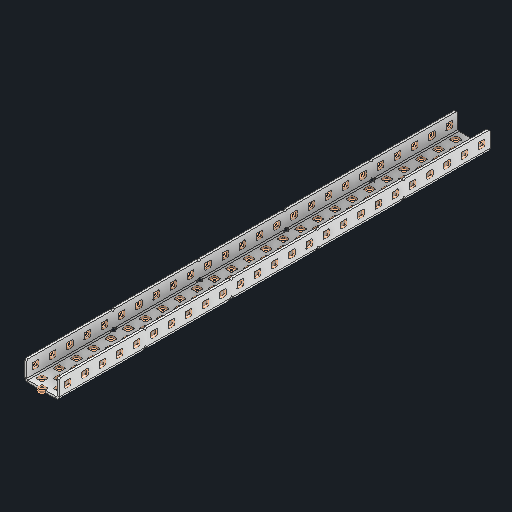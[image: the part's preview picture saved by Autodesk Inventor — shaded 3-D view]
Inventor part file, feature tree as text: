
AUTODESK INVENTOR PART (.ipt)
format: ipt  version: 2024 (Build 280153000, 153)  size: 2,036,224 bytes
history: native  units: in
note: dims shown in document units (in); Inventor stores cm internally (conversion verified against a paired STEP export)
features: other x256, sketch x5, sheet_metal_op x1
ambient origin geometry x8: Origin, YZ Plane, XZ Plane, XY Plane, X Axis, Y Axis, Z Axis, Center Point
bodies: Solid1 (feature_tree)
feature tree (262):
  other  "Alu C 1x2x1x25.ipt"
  other  "Solid1::Alu C 1x2x1x25.ipt"
  other  "TaggingFeature1"
  sketch  "Sketch1"  dims[d0=0.3937in]
  sketch  "Sketch2"  dims[d1=0.0625in]
  sketch  "Sketch3"
  other  "Flange Pattern Sketch"
  sketch  "Sketch9"
  sheet_metal_op  "Body Pattern Sketch"
  other  "Arc Length"
  sketch  "Sketch14"
  other  "Flange Pattern Plane"
  other  "Srf1"
  other  "Srf2"
  other  "Srf3"
  other  "Srf4"
  other  "Srf5"
  other  "Srf6"
  other  "Srf7"
  other  "Srf8"
  other  "Srf9"
  other  "Srf10"
  other  "Srf11"
  other  "Srf12"
  other  "Srf13"
  other  "Srf14"
  other  "Srf15"
  other  "Srf16"
  other  "Srf17"
  other  "Srf18"
  other  "Srf19"
  other  "Srf20"
  other  "Srf21"
  other  "Srf22"
  other  "Srf23"
  other  "Srf24"
  other  "Srf25"
  other  "Srf26"
  other  "Srf27"
  other  "Srf28"
  other  "Srf29"
  other  "Srf30"
  other  "Srf31"
  other  "Srf32"
  other  "Srf33"
  other  "Srf34"
  other  "Srf35"
  other  "Srf36"
  other  "Srf37"
  other  "Srf38"
  other  "Srf39"
  other  "Srf40"
  other  "Srf41"
  other  "Srf42"
  other  "Srf43"
  other  "Srf44"
  other  "Srf45"
  other  "Srf46"
  other  "Srf47"
  other  "Srf48"
  other  "Srf49"
  other  "Srf50"
  other  "Srf51"
  other  "Srf52"
  other  "Srf53"
  other  "Srf54"
  other  "Srf55"
  other  "Srf56"
  other  "Srf57"
  other  "Srf58"
  other  "Srf59"
  other  "Srf60"
  other  "Srf61"
  other  "Srf62"
  other  "Srf63"
  other  "Srf64"
  other  "Srf65"
  other  "Srf66"
  other  "Srf67"
  other  "Srf68"
  other  "Srf69"
  other  "Srf70"
  other  "Srf71"
  other  "Srf72"
  other  "Srf73"
  other  "Srf74"
  other  "Srf75"
  other  "Srf76"
  other  "Srf77"
  other  "Srf78"
  other  "Srf79"
  other  "Srf80"
  other  "Srf81"
  other  "Srf82"
  other  "Srf83"
  other  "Srf84"
  other  "Srf85"
  other  "Srf86"
  other  "Srf87"
  other  "Srf88"
  other  "Srf89"
  other  "Srf90"
  other  "Srf91"
  other  "Srf92"
  other  "Srf93"
  other  "Srf94"
  other  "Srf95"
  other  "Srf96"
  other  "Srf97"
  other  "Srf98"
  other  "Srf99"
  other  "Srf100"
  other  "Srf101"
  other  "Srf102"
  other  "Srf103"
  other  "Srf104"
  other  "Srf105"
  other  "Srf106"
  other  "Srf107"
  other  "Srf108"
  other  "Srf109"
  other  "Srf110"
  other  "Srf111"
  other  "Srf112"
  other  "Srf113"
  other  "Srf114"
  other  "Srf115"
  other  "Srf116"
  other  "Srf117"
  other  "Srf118"
  other  "Srf119"
  other  "Srf120"
  other  "Srf121"
  other  "Srf122"
  other  "Srf123"
  other  "Srf124"
  other  "Srf125"
  other  "Srf1::Derived"
  other  "Srf2::Derived"
  other  "Srf823::Derived"
  other  "Srf824::Derived"
  other  "Srf825::Derived"
  other  "Srf826::Derived"
  other  "Srf827::Derived"
  other  "Srf828::Derived"
  other  "Srf829::Derived"
  other  "Srf922::Derived"
  other  "Srf923::Derived"
  other  "Srf924::Derived"
  other  "Srf925::Derived"
  other  "Srf926::Derived"
  other  "Srf1143::Derived"
  other  "Srf1144::Derived"
  other  "Srf1145::Derived"
  other  "Srf1146::Derived"
  other  "Srf1147::Derived"
  other  "Srf1148::Derived"
  other  "Srf1149::Derived"
  other  "Srf1150::Derived"
  other  "Srf1151::Derived"
  other  "Srf1152::Derived"
  other  "Srf1153::Derived"
  other  "Srf1154::Derived"
  other  "Srf1155::Derived"
  other  "Srf1156::Derived"
  other  "Srf1157::Derived"
  other  "Srf1158::Derived"
  other  "Srf1159::Derived"
  other  "Srf1160::Derived"
  other  "Srf1161::Derived"
  other  "Srf1162::Derived"
  other  "Srf1163::Derived"
  other  "Srf1164::Derived"
  other  "Srf1165::Derived"
  other  "Srf1166::Derived"
  other  "Srf1167::Derived"
  other  "Srf1168::Derived"
  other  "Srf1169::Derived"
  other  "Srf1170::Derived"
  other  "Srf1171::Derived"
  other  "Srf1172::Derived"
  other  "Srf1173::Derived"
  other  "Srf1174::Derived"
  other  "Srf1175::Derived"
  other  "Srf1176::Derived"
  other  "Srf1177::Derived"
  other  "Srf1178::Derived"
  other  "Srf91::Derived"
  other  "Srf92::Derived"
  other  "Srf856::Derived"
  other  "Srf857::Derived"
  other  "Srf858::Derived"
  other  "Srf859::Derived"
  other  "Srf860::Derived"
  other  "Srf861::Derived"
  other  "Srf862::Derived"
  other  "Srf959::Derived"
  other  "Srf960::Derived"
  other  "Srf961::Derived"
  other  "Srf962::Derived"
  other  "Srf963::Derived"
  other  "Srf1199::Derived"
  other  "Srf1200::Derived"
  other  "Srf1201::Derived"
  other  "Srf1202::Derived"
  other  "Srf1203::Derived"
  other  "Srf1204::Derived"
  other  "Srf1205::Derived"
  other  "Srf1206::Derived"
  other  "Srf1207::Derived"
  other  "Srf1208::Derived"
  other  "Srf1209::Derived"
  other  "Srf1210::Derived"
  other  "Srf1211::Derived"
  other  "Srf1212::Derived"
  other  "Srf1213::Derived"
  other  "Srf1214::Derived"
  other  "Srf1215::Derived"
  other  "Srf1216::Derived"
  other  "Srf1217::Derived"
  other  "Srf1218::Derived"
  other  "Srf1219::Derived"
  other  "Srf1220::Derived"
  other  "Srf1221::Derived"
  other  "Srf1222::Derived"
  other  "Srf1223::Derived"
  other  "Srf1224::Derived"
  other  "Srf1225::Derived"
  other  "Srf1226::Derived"
  other  "Srf1227::Derived"
  other  "Srf1228::Derived"
  other  "Srf1229::Derived"
  other  "Srf1230::Derived"
  other  "Srf1231::Derived"
  other  "Srf1232::Derived"
  other  "Srf1233::Derived"
  other  "Srf1234::Derived"
  other  "Srf786::Derived"
  other  "Srf889::Derived"
  other  "Srf890::Derived"
  other  "Srf891::Derived"
  other  "Srf892::Derived"
  other  "Srf893::Derived"
  other  "Srf894::Derived"
  other  "Srf895::Derived"
  other  "Srf896::Derived"
  other  "Srf996::Derived"
  other  "Srf997::Derived"
  other  "Srf998::Derived"
  other  "Srf999::Derived"
  other  "Srf1000::Derived"
  other  "Srf1255::Derived"
  other  "Srf1256::Derived"
  other  "Srf1257::Derived"
  other  "Srf1258::Derived"
  other  "Srf1259::Derived"
  other  "Srf1260::Derived"
  other  "Srf1261::Derived"
  other  "Srf1262::Derived"
  other  "Srf1263::Derived"
  other  "Srf1264::Derived"
  other  "Srf1265::Derived"
